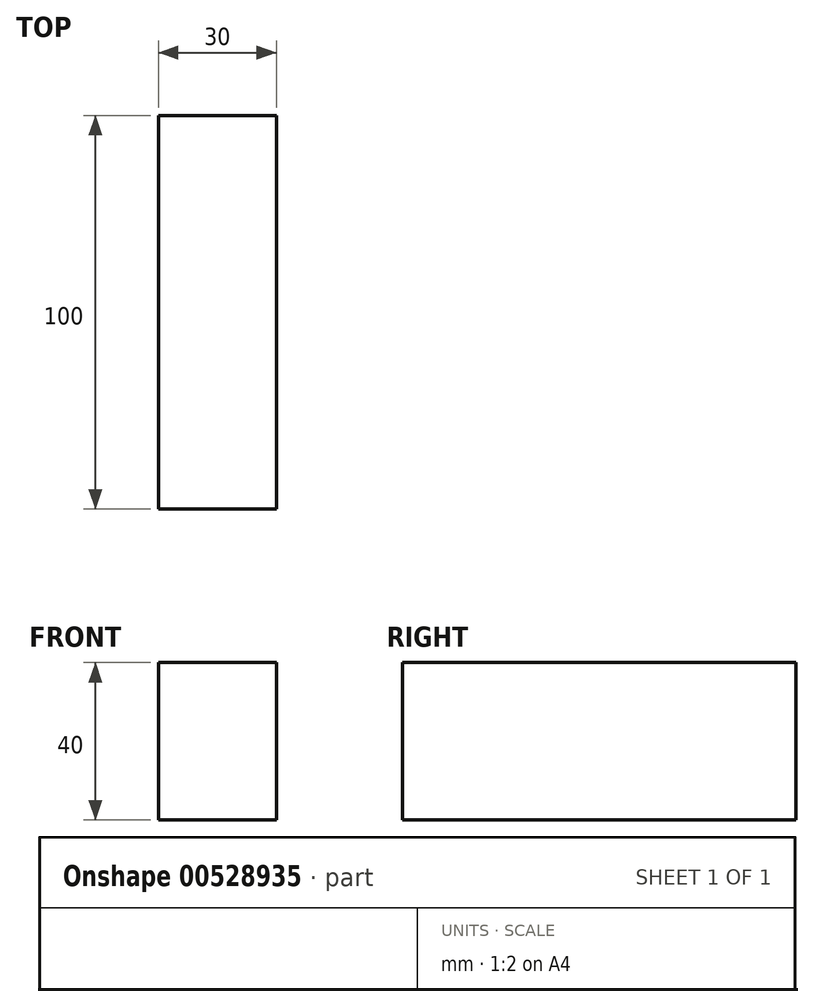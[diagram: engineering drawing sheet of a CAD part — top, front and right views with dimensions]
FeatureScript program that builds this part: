
annotation { "Feature Type Name" : "Feature", "Feature Type Description" : "" }
export const myFeature = defineFeature(function(context is Context, id is Id, definition is map)
    precondition{}
    {
        {
            var Q0;
            Q0=qCreatedBy(makeId("Top.planeOp"),FACE);
            var sketch = newSketch(context, id + "F0", { "sketchPlane" : qUnion([Q0])});
            skLineSegment(sketch, "E0.bottom", {"start": v(15, -50) * mm, "end": v(-15, -50) * mm});
            skLineSegment(sketch, "E0.top", {"start": v(15, 50) * mm, "end": v(-15, 50) * mm});
            skLineSegment(sketch, "E0.left", {"start": v(15, -50) * mm, "end": v(15, 50) * mm});
            skLineSegment(sketch, "E0.right", {"start": v(-15, -50) * mm, "end": v(-15, 50) * mm});
            skPoint(sketch, "E0.middle", {"position": v(0, 0) * mm});
            skSolve(sketch);
        }
        {
            var Q0;
            Q0 = qSketchRegion(id + "F0", true);
            extrude(context, id + "F1", {"entities" : qUnion([Q0]), "depth" : 40 * mm, "offsetDistance" : 25 * mm});
        }
    });
